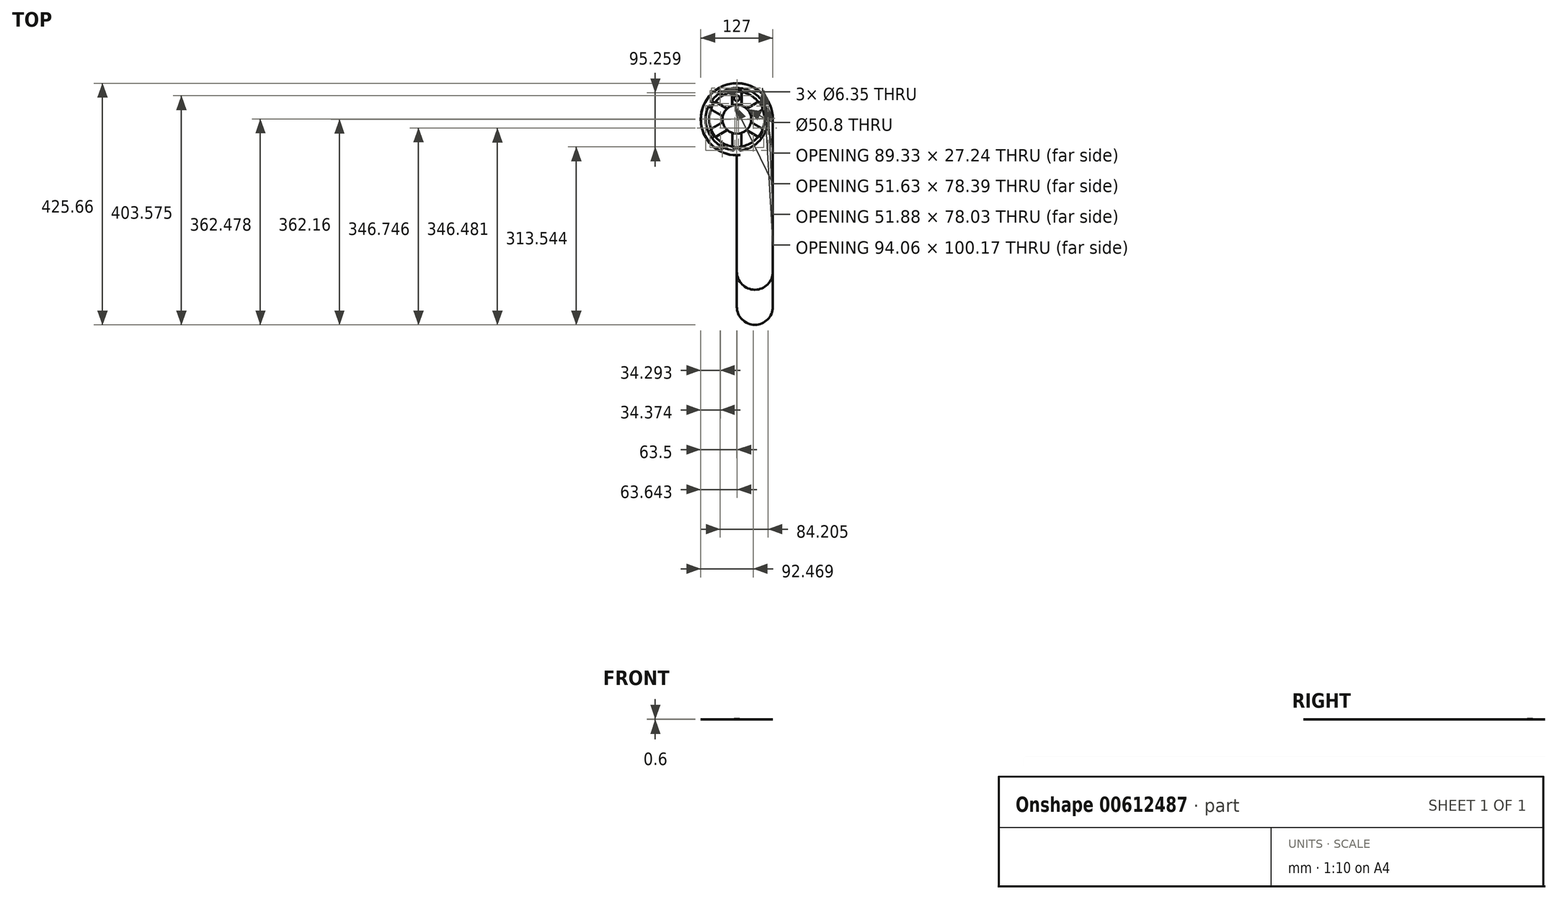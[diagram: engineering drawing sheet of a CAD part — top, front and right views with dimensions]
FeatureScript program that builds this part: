
annotation { "Feature Type Name" : "Feature", "Feature Type Description" : "" }
export const myFeature = defineFeature(function(context is Context, id is Id, definition is map)
    precondition{}
    {
        {
            assignVariable(context, id + "F0", {"name" : "e", "anyValue" : 0.3});
        }
        {
            var Q0;
            Q0=qCreatedBy(makeId("Top.planeOp"),FACE);
            var sketch = newSketch(context, id + "F1", { "sketchPlane" : qUnion([Q0])});
            skCircle(sketch, "E0", {"center": v(0, 0) * mm, "radius": 63.5 * mm});
            skCircle(sketch, "E1", {"center": v(0, 0) * mm, "radius": 25.4 * mm});
            skLineSegment(sketch, "E2.bottom", {"start": v(7.86, -24.37) * mm, "end": v(-7.86, -24.37) * mm});
            skLineSegment(sketch, "E2.top", {"start": v(7.86, -49.77) * mm, "end": v(-7.86, -49.77) * mm});
            skLineSegment(sketch, "E2.left", {"start": v(7.86, -24.37) * mm, "end": v(7.86, -49.77) * mm});
            skLineSegment(sketch, "E2.right", {"start": v(-7.86, -24.37) * mm, "end": v(-7.86, -49.77) * mm});
            skPoint(sketch, "E2.middle", {"position": v(0, -37.07) * mm});
            skCircle(sketch, "E3", {"center": v(0, -37.07) * mm, "radius": 4.87 * mm});
            skCircle(sketch, "E4.1.0", {"center": v(32.1, -18.53) * mm, "radius": 4.87 * mm});
            skLineSegment(sketch, "E4.1.1", {"start": v(25.03, -5.38) * mm, "end": v(47.03, -18.08) * mm});
            skLineSegment(sketch, "E4.1.2", {"start": v(17.17, -19) * mm, "end": v(39.17, -31.7) * mm});
            skLineSegment(sketch, "E4.1.3", {"start": v(25.03, -5.38) * mm, "end": v(17.17, -19) * mm});
            skLineSegment(sketch, "E4.1.4", {"start": v(47.03, -18.08) * mm, "end": v(39.17, -31.7) * mm});
            skCircle(sketch, "E4.2.0", {"center": v(32.1, 18.53) * mm, "radius": 4.87 * mm});
            skLineSegment(sketch, "E4.2.1", {"start": v(17.17, 19) * mm, "end": v(39.17, 31.7) * mm});
            skLineSegment(sketch, "E4.2.2", {"start": v(25.03, 5.38) * mm, "end": v(47.03, 18.08) * mm});
            skLineSegment(sketch, "E4.2.3", {"start": v(17.17, 19) * mm, "end": v(25.03, 5.38) * mm});
            skLineSegment(sketch, "E4.2.4", {"start": v(39.17, 31.7) * mm, "end": v(47.03, 18.08) * mm});
            skCircle(sketch, "E4.3.0", {"center": v(0, 37.07) * mm, "radius": 4.87 * mm});
            skLineSegment(sketch, "E4.3.1", {"start": v(-7.86, 24.37) * mm, "end": v(-7.86, 49.77) * mm});
            skLineSegment(sketch, "E4.3.2", {"start": v(7.86, 24.37) * mm, "end": v(7.86, 49.77) * mm});
            skLineSegment(sketch, "E4.3.3", {"start": v(-7.86, 24.37) * mm, "end": v(7.86, 24.37) * mm});
            skLineSegment(sketch, "E4.3.4", {"start": v(-7.86, 49.77) * mm, "end": v(7.86, 49.77) * mm});
            skCircle(sketch, "E4.4.0", {"center": v(-32.1, 18.53) * mm, "radius": 4.87 * mm});
            skLineSegment(sketch, "E4.4.1", {"start": v(-25.03, 5.38) * mm, "end": v(-47.03, 18.08) * mm});
            skLineSegment(sketch, "E4.4.2", {"start": v(-17.17, 19) * mm, "end": v(-39.17, 31.7) * mm});
            skLineSegment(sketch, "E4.4.3", {"start": v(-25.03, 5.38) * mm, "end": v(-17.17, 19) * mm});
            skLineSegment(sketch, "E4.4.4", {"start": v(-47.03, 18.08) * mm, "end": v(-39.17, 31.7) * mm});
            skCircle(sketch, "E4.5.0", {"center": v(-32.1, -18.53) * mm, "radius": 4.87 * mm});
            skLineSegment(sketch, "E4.5.1", {"start": v(-17.17, -19) * mm, "end": v(-39.17, -31.7) * mm});
            skLineSegment(sketch, "E4.5.2", {"start": v(-25.03, -5.38) * mm, "end": v(-47.03, -18.08) * mm});
            skLineSegment(sketch, "E4.5.3", {"start": v(-17.17, -19) * mm, "end": v(-25.03, -5.38) * mm});
            skLineSegment(sketch, "E4.5.4", {"start": v(-39.17, -31.7) * mm, "end": v(-47.03, -18.08) * mm});
            skCircle(sketch, "E5", {"center": v(-29.2, 46.64) * mm, "radius": 3.18 * mm});
            skCircle(sketch, "E6.1.0", {"center": v(-25.8, -48.62) * mm, "radius": 3.18 * mm});
            skCircle(sketch, "E6.2.0", {"center": v(55, 1.97) * mm, "radius": 3.18 * mm});
            skLineSegment(sketch, "E7.bottom", {"start": v(8.5, 23.73) * mm, "end": v(-8.5, 23.73) * mm});
            skLineSegment(sketch, "E7.top", {"start": v(8.5, 50.4) * mm, "end": v(-8.5, 50.4) * mm});
            skLineSegment(sketch, "E7.left", {"start": v(8.5, 23.73) * mm, "end": v(8.5, 50.4) * mm});
            skLineSegment(sketch, "E7.right", {"start": v(-8.5, 23.73) * mm, "end": v(-8.5, 50.4) * mm});
            skLineSegment(sketch, "E8", {"start": v(63.5, 0) * mm, "end": v(63.5, -268.6) * mm});
            skLineSegment(sketch, "E9", {"start": v(0, -63.5) * mm, "end": v(0, -268.6) * mm});
            skLineSegment(sketch, "E10", {"start": v(0, -268.6) * mm, "end": v(63.5, -268.6) * mm});
            skCircle(sketch, "E11", {"center": v(31.75, -268.6) * mm, "radius": 31.75 * mm});
            skSolve(sketch);
        }
        {
            var Q0;
            Q0=makeQuery(id+"F1.imprint","IMPRINT",FACE,{"disambiguationData":[TD([[makeQuery(id+"F1.imprint","IMPRINT",EDGE,{"derivedFrom":sQuery(id+"F1.wireOp",EDGE,"E2.top")}),1.0]])]});
            var Q1;
            {var subQ0=sQuery(id+"F1.wireOp",EDGE,"E8");Q1=makeQuery(id+"F1.imprint","IMPRINT",FACE,{"disambiguationData":[TD([[makeQuery(id+"F1.imprint","IMPRINT",EDGE,{"derivedFrom":subQ0}),-1.0]])]});}
            var Q2;
            {var subQ0=sQuery(id+"F1.wireOp",EDGE,"E10");Q2=makeQuery(id+"F1.imprint","IMPRINT",FACE,{"disambiguationData":[TD([[makeQuery(id+"F1.imprint","IMPRINT",EDGE,{"derivedFrom":subQ0}),1.0]])]});}
            var Q3;
            {var subQ0=sQuery(id+"F1.wireOp",EDGE,"E10");Q3=makeQuery(id+"F1.imprint","IMPRINT",FACE,{"disambiguationData":[TD([[makeQuery(id+"F1.imprint","IMPRINT",EDGE,{"derivedFrom":subQ0}),-1.0]])]});}
            extrude(context, id + "F2", {"entities" : qUnion([Q0, Q1, Q2, Q3]), "depth" : (getVariable(context, 'e')) * mm, "offsetDistance" : 25.4 * mm});
        }
        {
            var Q0;
            Q0=makeQuery(id+"F1.imprint","IMPRINT",FACE,{"disambiguationData":[TD([[makeQuery(id+"F1.imprint","IMPRINT",EDGE,{"derivedFrom":sQuery(id+"F1.wireOp",EDGE,"E4.3.0")}),-1.0]])]});
            var Q1;
            Q1=makeQuery(id+"F1.imprint","IMPRINT",FACE,{"disambiguationData":[TD([[makeQuery(id+"F1.imprint","IMPRINT",EDGE,{"derivedFrom":sQuery(id+"F1.wireOp",EDGE,"E4.3.0")}),1.0]])]});
            extrude(context, id + "F3", {"entities" : qUnion([Q0, Q1]), "depth" : (getVariable(context, 'e')) * mm, "offsetDistance" : 25.4 * mm});
        }
        {
            var Q0;
            Q0=makeQuery(id+"F1.imprint","IMPRINT",FACE,{"disambiguationData":[TD([[makeQuery(id+"F1.imprint","IMPRINT",EDGE,{"derivedFrom":sQuery(id+"F1.wireOp",EDGE,"E4.3.0")}),1.0]])]});
            extrude(context, id + "F4", {"entities" : qUnion([Q0]), "operationType" : NewBodyOperationType.ADD, "depth" : 2 * (getVariable(context, 'e')) * mm, "offsetDistance" : 25.4 * mm});
        }
        {
            var Q0;
            Q0=qCreatedBy(makeId("Top.planeOp"),FACE);
            var sketch = newSketch(context, id + "F5", { "sketchPlane" : qUnion([Q0])});
            skCircle(sketch, "E12", {"center": v(0, 0) * mm, "radius": 63.5 * mm});
            skCircle(sketch, "E13", {"center": v(0, 0) * mm, "radius": 25.4 * mm});
            skLineSegment(sketch, "E14", {"start": v(63.5, 0) * mm, "end": v(63.5, -330.4) * mm});
            skLineSegment(sketch, "E15", {"start": v(63.5, -330.4) * mm, "end": v(0, -330.4) * mm});
            skLineSegment(sketch, "E16", {"start": v(0, -330.4) * mm, "end": v(0, -63.5) * mm});
            skCircle(sketch, "E17", {"center": v(31.75, -330.4) * mm, "radius": 31.75 * mm});
            skCircle(sketch, "E18", {"center": v(0, 0) * mm, "radius": 55.03 * mm});
            skCircle(sketch, "E19", {"center": v(0, 0) * mm, "radius": 48.68 * mm});
            skLineSegment(sketch, "E20.bottom", {"start": v(-6.46, 0) * mm, "end": v(5.97, 0) * mm});
            skLineSegment(sketch, "E20.top", {"start": v(-6.46, -63.22) * mm, "end": v(5.97, -63.22) * mm});
            skLineSegment(sketch, "E20.left", {"start": v(-6.46, 0) * mm, "end": v(-6.46, -63.22) * mm});
            skLineSegment(sketch, "E20.right", {"start": v(5.97, 0) * mm, "end": v(5.97, -63.22) * mm});
            skLineSegment(sketch, "E21.1.0", {"start": v(-2.99, 5.17) * mm, "end": v(51.76, 36.78) * mm});
            skLineSegment(sketch, "E21.1.1", {"start": v(3.23, -5.6) * mm, "end": v(57.98, 26.02) * mm});
            skLineSegment(sketch, "E21.2.0", {"start": v(-2.99, -5.17) * mm, "end": v(-57.73, 26.44) * mm});
            skLineSegment(sketch, "E21.2.1", {"start": v(3.23, 5.6) * mm, "end": v(-51.52, 37.2) * mm});
            skPoint(sketch, "E22", {"position": v(50.56, 21.73) * mm});
            skPoint(sketch, "E23", {"position": v(45.02, 18.53) * mm});
            skPoint(sketch, "E24", {"position": v(5.97, -54.7) * mm});
            skPoint(sketch, "E25", {"position": v(5.97, -48.32) * mm});
            skPoint(sketch, "E26", {"position": v(-6.46, -48.25) * mm});
            skPoint(sketch, "E27", {"position": v(-6.46, -54.65) * mm});
            skPoint(sketch, "E28", {"position": v(-44.1, 32.92) * mm});
            skPoint(sketch, "E29", {"position": v(-38.56, 29.72) * mm});
            skPoint(sketch, "E30", {"position": v(-44.83, 18.99) * mm});
            skPoint(sketch, "E31", {"position": v(-50.36, 22.18) * mm});
            skPoint(sketch, "E32", {"position": v(44.4, 32.53) * mm});
            skPoint(sketch, "E33", {"position": v(38.86, 29.33) * mm});
            skCircle(sketch, "E34", {"center": v(41.63, 30.93) * mm, "radius": 3.2 * mm});
            skPoint(sketch, "E34.third.point", {"position": v(44.4, 29.33) * mm});
            skCircle(sketch, "E35", {"center": v(47.79, 20.13) * mm, "radius": 3.2 * mm});
            skPoint(sketch, "E35.third.point", {"position": v(45.02, 21.73) * mm});
            skCircle(sketch, "E36", {"center": v(-41.33, 31.32) * mm, "radius": 3.2 * mm});
            skPoint(sketch, "E36.third.point", {"position": v(-38.56, 32.92) * mm});
            skCircle(sketch, "E37", {"center": v(-47.6, 20.58) * mm, "radius": 3.2 * mm});
            skPoint(sketch, "E37.third.point", {"position": v(-44.83, 22.18) * mm});
            skCircle(sketch, "E38", {"center": v(-6.48, -51.45) * mm, "radius": 3.2 * mm});
            skPoint(sketch, "E38.third.point", {"position": v(-9.5, -50.4) * mm});
            skCircle(sketch, "E39", {"center": v(6.18, -51.51) * mm, "radius": 3.2 * mm});
            skPoint(sketch, "E39.third.point", {"position": v(9.28, -50.7) * mm});
            skSolve(sketch);
        }
        {
            var Q0;
            {var subQ0=sQuery(id+"F5.wireOp",EDGE,"E21.1.0");var subQ1=sQuery(id+"F5.wireOp",EDGE,"E12");var subQ2=makeQuery(id+"F5.imprint","INTERSECT",VERTEX,{"derivedFrom":[subQ1,subQ0]});Q0=makeQuery(id+"F5.imprint","IMPRINT",FACE,{"disambiguationData":[TD([[makeQuery(id+"F5.imprint","IMPRINT",EDGE,{"disambiguationData":[TD([[subQ2,-1.0]])],"derivedFrom":subQ1}),1.0]])]});}
            var Q1;
            {var subQ0=sQuery(id+"F5.wireOp",EDGE,"E21.2.0");var subQ1=sQuery(id+"F5.wireOp",EDGE,"E12");var subQ2=makeQuery(id+"F5.imprint","INTERSECT",VERTEX,{"derivedFrom":[subQ1,subQ0]});Q1=makeQuery(id+"F5.imprint","IMPRINT",FACE,{"disambiguationData":[TD([[makeQuery(id+"F5.imprint","IMPRINT",EDGE,{"disambiguationData":[TD([[subQ2,1.0]])],"derivedFrom":subQ1}),1.0]])]});}
            var Q2;
            {var subQ1=sQuery(id+"F5.wireOp",EDGE,"E12");var subQ9=sQuery(id+"F5.wireOp",EDGE,"E21.2.0");var subQ10=makeQuery(id+"F5.imprint","INTERSECT",VERTEX,{"derivedFrom":[subQ1,subQ9]});Q2=makeQuery(id+"F5.imprint","IMPRINT",FACE,{"disambiguationData":[TD([[makeQuery(id+"F5.imprint","IMPRINT",EDGE,{"disambiguationData":[TD([[subQ10,-1.0]])],"derivedFrom":subQ1}),1.0]])]});}
            var Q3;
            {var subQ0=sQuery(id+"F5.wireOp",EDGE,"E21.1.1");var subQ1=sQuery(id+"F5.wireOp",EDGE,"E13");var subQ2=makeQuery(id+"F5.imprint","INTERSECT",VERTEX,{"derivedFrom":[subQ1,subQ0]});Q3=makeQuery(id+"F5.imprint","IMPRINT",FACE,{"disambiguationData":[TD([[makeQuery(id+"F5.imprint","IMPRINT",EDGE,{"disambiguationData":[TD([[subQ2,1.0]])],"derivedFrom":subQ1}),-1.0]])]});}
            var Q4;
            {var subQ0=sQuery(id+"F5.wireOp",EDGE,"E21.2.0");var subQ1=sQuery(id+"F5.wireOp",EDGE,"E13");var subQ2=makeQuery(id+"F5.imprint","INTERSECT",VERTEX,{"derivedFrom":[subQ1,subQ0]});Q4=makeQuery(id+"F5.imprint","IMPRINT",FACE,{"disambiguationData":[TD([[makeQuery(id+"F5.imprint","IMPRINT",EDGE,{"disambiguationData":[TD([[subQ2,-1.0]])],"derivedFrom":subQ1}),-1.0]])]});}
            var Q5;
            {var subQ0=sQuery(id+"F5.wireOp",EDGE,"E21.1.0");var subQ1=sQuery(id+"F5.wireOp",EDGE,"E13");var subQ2=makeQuery(id+"F5.imprint","INTERSECT",VERTEX,{"derivedFrom":[subQ1,subQ0]});Q5=makeQuery(id+"F5.imprint","IMPRINT",FACE,{"disambiguationData":[TD([[makeQuery(id+"F5.imprint","IMPRINT",EDGE,{"disambiguationData":[TD([[subQ2,-1.0]])],"derivedFrom":subQ1}),-1.0]])]});}
            var Q6;
            {var subQ1=sQuery(id+"F5.wireOp",EDGE,"E13");var subQ9=sQuery(id+"F5.wireOp",EDGE,"E21.2.1");var subQ10=makeQuery(id+"F5.imprint","INTERSECT",VERTEX,{"derivedFrom":[subQ1,subQ9]});Q6=makeQuery(id+"F5.imprint","IMPRINT",FACE,{"disambiguationData":[TD([[makeQuery(id+"F5.imprint","IMPRINT",EDGE,{"disambiguationData":[TD([[subQ10,-1.0]])],"derivedFrom":subQ1}),-1.0]])]});}
            var Q7;
            {var subQ1=sQuery(id+"F5.wireOp",EDGE,"E13");var subQ9=sQuery(id+"F5.wireOp",EDGE,"E21.1.0");var subQ10=makeQuery(id+"F5.imprint","INTERSECT",VERTEX,{"derivedFrom":[subQ1,subQ9]});Q7=makeQuery(id+"F5.imprint","IMPRINT",FACE,{"disambiguationData":[TD([[makeQuery(id+"F5.imprint","IMPRINT",EDGE,{"disambiguationData":[TD([[subQ10,1.0]])],"derivedFrom":subQ1}),-1.0]])]});}
            var Q8;
            {var subQ1=sQuery(id+"F5.wireOp",EDGE,"E13");var subQ6=sQuery(id+"F5.wireOp",EDGE,"E20.left");var subQ7=makeQuery(id+"F5.imprint","INTERSECT",VERTEX,{"derivedFrom":[subQ1,subQ6]});Q8=makeQuery(id+"F5.imprint","IMPRINT",FACE,{"disambiguationData":[TD([[makeQuery(id+"F5.imprint","IMPRINT",EDGE,{"disambiguationData":[TD([[subQ7,-1.0]])],"derivedFrom":subQ1}),-1.0]])]});}
            var Q9;
            {var subQ1=sQuery(id+"F5.wireOp",EDGE,"E12");var subQ9=makeQuery(id+"F5.imprint","INTERSECT",VERTEX,{"derivedFrom":[subQ1,sQuery(id+"F5.wireOp",EDGE,"E14")]});Q9=makeQuery(id+"F5.imprint","IMPRINT",FACE,{"disambiguationData":[TD([[makeQuery(id+"F5.imprint","IMPRINT",EDGE,{"disambiguationData":[TD([[subQ9,-1.0]])],"derivedFrom":subQ1}),1.0]])]});}
            var Q10;
            {var subQ0=sQuery(id+"F5.wireOp",EDGE,"E20.left");var subQ1=sQuery(id+"F5.wireOp",EDGE,"E12");var subQ2=makeQuery(id+"F5.imprint","INTERSECT",VERTEX,{"derivedFrom":[subQ1,subQ0]});Q10=makeQuery(id+"F5.imprint","IMPRINT",FACE,{"disambiguationData":[TD([[makeQuery(id+"F5.imprint","IMPRINT",EDGE,{"disambiguationData":[TD([[subQ2,-1.0]])],"derivedFrom":subQ1}),1.0]])]});}
            var Q11;
            {var subQ0=sQuery(id+"F5.wireOp",EDGE,"E38");var subQ5=sQuery(id+"F5.wireOp",EDGE,"E19");var subQ6=makeQuery(id+"F5.imprint","INTERSECT",VERTEX,{"derivedFrom":[subQ5,subQ0]});Q11=makeQuery(id+"F5.imprint","IMPRINT",FACE,{"disambiguationData":[TD([[makeQuery(id+"F5.imprint","IMPRINT",EDGE,{"disambiguationData":[TD([[subQ6,-1.0]])],"derivedFrom":subQ5}),-1.0]])]});}
            var Q12;
            {var subQ0=sQuery(id+"F5.wireOp",EDGE,"E21.1.0");var subQ1=sQuery(id+"F5.wireOp",EDGE,"E12");var subQ2=makeQuery(id+"F5.imprint","INTERSECT",VERTEX,{"derivedFrom":[subQ1,subQ0]});Q12=makeQuery(id+"F5.imprint","IMPRINT",FACE,{"disambiguationData":[TD([[makeQuery(id+"F5.imprint","IMPRINT",EDGE,{"disambiguationData":[TD([[subQ2,1.0]])],"derivedFrom":subQ1}),1.0]])]});}
            var Q13;
            {var subQ0=sQuery(id+"F5.wireOp",EDGE,"E35");var subQ5=sQuery(id+"F5.wireOp",EDGE,"E19");var subQ6=makeQuery(id+"F5.imprint","INTERSECT",VERTEX,{"derivedFrom":[subQ5,subQ0]});Q13=makeQuery(id+"F5.imprint","IMPRINT",FACE,{"disambiguationData":[TD([[makeQuery(id+"F5.imprint","IMPRINT",EDGE,{"disambiguationData":[TD([[subQ6,-1.0]])],"derivedFrom":subQ5}),-1.0]])]});}
            var Q14;
            {var subQ0=sQuery(id+"F5.wireOp",EDGE,"E36");var subQ5=sQuery(id+"F5.wireOp",EDGE,"E19");var subQ6=makeQuery(id+"F5.imprint","INTERSECT",VERTEX,{"derivedFrom":[subQ5,subQ0]});Q14=makeQuery(id+"F5.imprint","IMPRINT",FACE,{"disambiguationData":[TD([[makeQuery(id+"F5.imprint","IMPRINT",EDGE,{"disambiguationData":[TD([[subQ6,-1.0]])],"derivedFrom":subQ5}),-1.0]])]});}
            var Q15;
            {var subQ0=sQuery(id+"F5.wireOp",EDGE,"E14");Q15=makeQuery(id+"F5.imprint","IMPRINT",FACE,{"disambiguationData":[TD([[makeQuery(id+"F5.imprint","IMPRINT",EDGE,{"derivedFrom":subQ0}),-1.0]])]});}
            var Q16;
            {var subQ0=sQuery(id+"F5.wireOp",EDGE,"E15");Q16=makeQuery(id+"F5.imprint","IMPRINT",FACE,{"disambiguationData":[TD([[makeQuery(id+"F5.imprint","IMPRINT",EDGE,{"derivedFrom":subQ0}),-1.0]])]});}
            var Q17;
            {var subQ0=sQuery(id+"F5.wireOp",EDGE,"E15");Q17=makeQuery(id+"F5.imprint","IMPRINT",FACE,{"disambiguationData":[TD([[makeQuery(id+"F5.imprint","IMPRINT",EDGE,{"derivedFrom":subQ0}),1.0]])]});}
            extrude(context, id + "F6", {"entities" : qUnion([Q0, Q1, Q2, Q3, Q4, Q5, Q6, Q7, Q8, Q9, Q10, Q11, Q12, Q13, Q14, Q15, Q16, Q17]), "depth" : (getVariable(context, 'e')) * mm, "offsetDistance" : 25.4 * mm});
        }
    });
